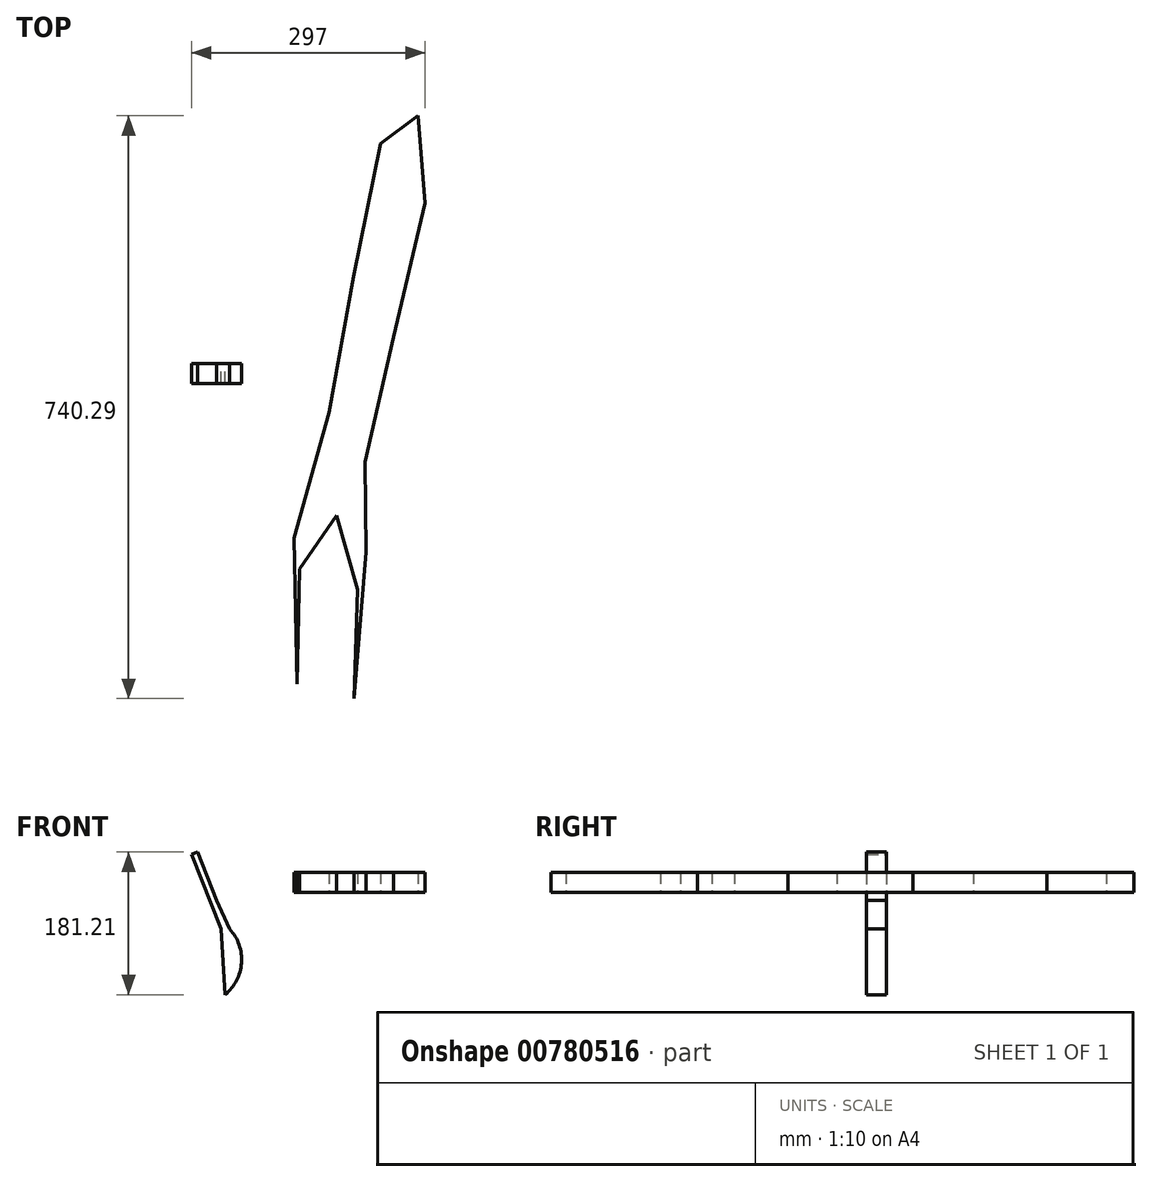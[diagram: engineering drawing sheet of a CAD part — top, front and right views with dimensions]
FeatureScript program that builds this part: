
annotation { "Feature Type Name" : "Feature", "Feature Type Description" : "" }
export const myFeature = defineFeature(function(context is Context, id is Id, definition is map)
    precondition{}
    {
        {
            var Q0;
            Q0=qCreatedBy(makeId("Top.planeOp"),FACE);
            var sketch = newSketch(context, id + "F0", { "sketchPlane" : qUnion([Q0])});
            skLineSegment(sketch, "E0", {"start": v(122.2, -125.4) * mm, "end": v(158.03, 33.4) * mm});
            skLineSegment(sketch, "E1", {"start": v(158.03, 33.4) * mm, "end": v(198.47, 203.77) * mm});
            skLineSegment(sketch, "E2", {"start": v(198.47, 203.77) * mm, "end": v(189.5, 314.45) * mm});
            skLineSegment(sketch, "E3", {"start": v(189.5, 314.45) * mm, "end": v(141.97, 279.25) * mm});
            skLineSegment(sketch, "E4", {"start": v(141.97, 279.25) * mm, "end": v(107.62, 110.4) * mm});
            skLineSegment(sketch, "E5", {"start": v(107.62, 110.4) * mm, "end": v(76.19, -62.72) * mm});
            skLineSegment(sketch, "E6", {"start": v(76.19, -62.72) * mm, "end": v(31.7, -221.64) * mm});
            skLineSegment(sketch, "E7", {"start": v(31.7, -221.64) * mm, "end": v(35.4, -407.23) * mm});
            skLineSegment(sketch, "E8", {"start": v(35.4, -407.23) * mm, "end": v(38.7, -261.56) * mm});
            skLineSegment(sketch, "E9", {"start": v(38.7, -261.56) * mm, "end": v(85.7, -193.09) * mm});
            skLineSegment(sketch, "E10", {"start": v(85.7, -193.09) * mm, "end": v(112.15, -287.33) * mm});
            skLineSegment(sketch, "E11", {"start": v(112.15, -287.33) * mm, "end": v(108.1, -425.84) * mm});
            skLineSegment(sketch, "E12", {"start": v(108.1, -425.84) * mm, "end": v(123, -239.87) * mm});
            skLineSegment(sketch, "E13", {"start": v(123, -239.87) * mm, "end": v(122.2, -125.4) * mm});
            skSolve(sketch);
        }
        {
            var Q0;
            Q0 = qSketchRegion(id + "F0", true);
            extrude(context, id + "F1", {"entities" : qUnion([Q0]), "depth" : 25.4 * mm, "offsetDistance" : 25.4 * mm});
        }
        {
            var Q0;
            Q0=qCreatedBy(makeId("Front.planeOp"),FACE);
            var sketch = newSketch(context, id + "F2", { "sketchPlane" : qUnion([Q0])});
            skLineSegment(sketch, "E14", {"start": v(-90.83, 51.06) * mm, "end": v(-66.56, -10.2) * mm});
            skLineSegment(sketch, "E15", {"start": v(-66.56, -10.2) * mm, "end": v(-49.91, -46.84) * mm});
            skArc(sketch, "E16", {"start": v(-55.7, -130.15) * mm, "mid": v(-34.92, -89.74) * mm, "end": v(-49.91, -46.84) * mm});
            skLineSegment(sketch, "E17", {"start": v(-90.83, 51.06) * mm, "end": v(-98.53, 48) * mm});
            skLineSegment(sketch, "E18", {"start": v(-98.53, 48) * mm, "end": v(-60.96, -46.84) * mm});
            skLineSegment(sketch, "E19", {"start": v(-60.96, -46.84) * mm, "end": v(-55.7, -130.15) * mm});
            skSolve(sketch);
        }
        {
            var Q0;
            Q0 = qSketchRegion(id + "F2", true);
            extrude(context, id + "F3", {"entities" : qUnion([Q0]), "depth" : 25.4 * mm, "offsetDistance" : 25.4 * mm});
        }
    });
